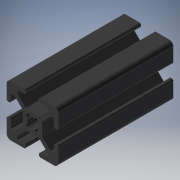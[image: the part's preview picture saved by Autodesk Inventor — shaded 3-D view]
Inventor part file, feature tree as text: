
AUTODESK INVENTOR PART (.ipt)
format: ipt  version: 2025 (Build 290162000, 162)  size: 239,104 bytes
history: native  units: mm
features: extrude x1, sketch x1
ambient origin geometry x8: Origin, YZ Plane, XZ Plane, XY Plane, X Axis, Y Axis, Z Axis, Center Point
bodies: Solid1 (feature_tree)
feature tree (2):
  extrude  "Extrusion1"  [1 undecoded]
  sketch  "Sketch_1"  dims[d0=45.0mm d1=0.0mm]
note: 1 required parameter value undecoded (feature->parameter linkage not recoverable at this tier; creation-order binding heuristic only, values carry confidence <= 0.55)
